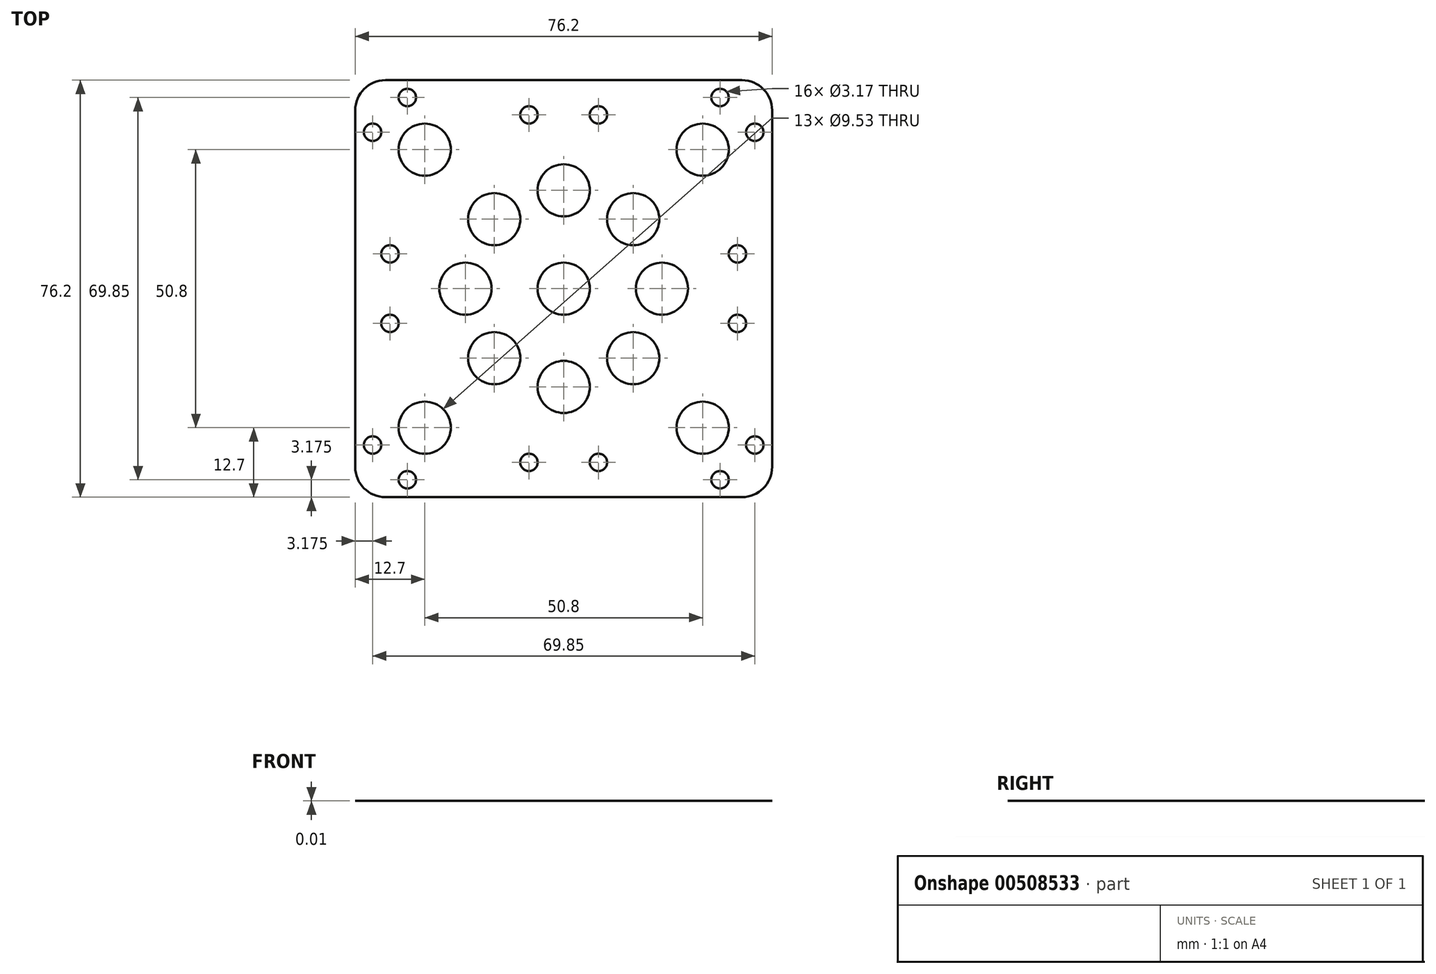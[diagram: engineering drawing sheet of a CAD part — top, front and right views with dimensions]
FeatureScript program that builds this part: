
annotation { "Feature Type Name" : "Feature", "Feature Type Description" : "" }
export const myFeature = defineFeature(function(context is Context, id is Id, definition is map)
    precondition{}
    {
        {
            var Q0;
            Q0=qCreatedBy(makeId("Top.planeOp"),FACE);
            var sketch = newSketch(context, id + "F0", { "sketchPlane" : qUnion([Q0])});
            skLineSegment(sketch, "E0.bottom", {"start": v(38.1, 38.1) * mm, "end": v(-38.1, 38.1) * mm});
            skLineSegment(sketch, "E0.top", {"start": v(38.1, -38.1) * mm, "end": v(-38.1, -38.1) * mm});
            skLineSegment(sketch, "E0.left", {"start": v(38.1, 38.1) * mm, "end": v(38.1, -38.1) * mm});
            skLineSegment(sketch, "E0.right", {"start": v(-38.1, 38.1) * mm, "end": v(-38.1, -38.1) * mm});
            skPoint(sketch, "E0.middle", {"position": v(0, 0) * mm});
            skLineSegment(sketch, "E1.bottom", {"start": v(-25.4, 25.4) * mm, "end": v(25.4, 25.4) * mm, "construction": true});
            skLineSegment(sketch, "E1.top", {"start": v(-25.4, -25.4) * mm, "end": v(25.4, -25.4) * mm, "construction": true});
            skLineSegment(sketch, "E1.left", {"start": v(-25.4, 25.4) * mm, "end": v(-25.4, -25.4) * mm, "construction": true});
            skLineSegment(sketch, "E1.right", {"start": v(25.4, 25.4) * mm, "end": v(25.4, -25.4) * mm, "construction": true});
            skCircle(sketch, "E2", {"center": v(-25.4, 25.4) * mm, "radius": 4.76 * mm});
            skCircle(sketch, "E3", {"center": v(25.4, 25.4) * mm, "radius": 4.76 * mm});
            skCircle(sketch, "E4", {"center": v(25.4, -25.4) * mm, "radius": 4.76 * mm});
            skCircle(sketch, "E5", {"center": v(-25.4, -25.4) * mm, "radius": 4.76 * mm});
            skLineSegment(sketch, "E6.bottom", {"start": v(12.7, 12.7) * mm, "end": v(-12.7, 12.7) * mm, "construction": true});
            skLineSegment(sketch, "E6.top", {"start": v(12.7, -12.7) * mm, "end": v(-12.7, -12.7) * mm, "construction": true});
            skLineSegment(sketch, "E6.left", {"start": v(12.7, 12.7) * mm, "end": v(12.7, -12.7) * mm, "construction": true});
            skLineSegment(sketch, "E6.right", {"start": v(-12.7, 12.7) * mm, "end": v(-12.7, -12.7) * mm, "construction": true});
            skCircle(sketch, "E7", {"center": v(-12.7, 12.7) * mm, "radius": 4.76 * mm});
            skCircle(sketch, "E8", {"center": v(12.7, 12.7) * mm, "radius": 4.76 * mm});
            skCircle(sketch, "E9", {"center": v(12.7, -12.7) * mm, "radius": 4.76 * mm});
            skCircle(sketch, "E10", {"center": v(-12.7, -12.7) * mm, "radius": 4.76 * mm});
            skLineSegment(sketch, "E11", {"start": v(-12.7, 12.7) * mm, "end": v(-38.1, 0) * mm, "construction": true});
            skLineSegment(sketch, "E12", {"start": v(-38.1, 0) * mm, "end": v(-12.7, -12.7) * mm, "construction": true});
            skLineSegment(sketch, "E13", {"start": v(-25.4, 6.35) * mm, "end": v(-38.1, 6.35) * mm, "construction": true});
            skLineSegment(sketch, "E14", {"start": v(-25.4, -6.35) * mm, "end": v(-38.1, -6.35) * mm, "construction": true});
            skPoint(sketch, "E15", {"position": v(-31.75, 6.35) * mm});
            skPoint(sketch, "E16", {"position": v(-31.75, -6.35) * mm});
            skCircle(sketch, "E17", {"center": v(-31.75, 6.35) * mm, "radius": 1.59 * mm});
            skCircle(sketch, "E18", {"center": v(-31.75, -6.35) * mm, "radius": 1.59 * mm});
            skCircle(sketch, "E19.MirrorC", {"center": v(31.75, 6.35) * mm, "radius": 1.59 * mm});
            skCircle(sketch, "E20.MirrorC", {"center": v(31.75, -6.35) * mm, "radius": 1.59 * mm});
            skLineSegment(sketch, "E21", {"start": v(-12.7, 12.7) * mm, "end": v(0, 38.1) * mm, "construction": true});
            skLineSegment(sketch, "E22", {"start": v(-6.35, 25.4) * mm, "end": v(-6.35, 38.1) * mm, "construction": true});
            skCircle(sketch, "E23", {"center": v(-6.35, 31.75) * mm, "radius": 1.59 * mm});
            skCircle(sketch, "E24.MirrorC", {"center": v(6.35, 31.75) * mm, "radius": 1.59 * mm});
            skCircle(sketch, "E25.MirrorC", {"center": v(-6.35, -31.75) * mm, "radius": 1.59 * mm});
            skCircle(sketch, "E26.MirrorC", {"center": v(6.35, -31.75) * mm, "radius": 1.59 * mm});
            skCircle(sketch, "E27", {"center": v(0, 0) * mm, "radius": 4.76 * mm});
            skLineSegment(sketch, "E28", {"start": v(-25.4, 25.4) * mm, "end": v(-38.1, 38.1) * mm, "construction": true});
            skCircle(sketch, "E29.cCircle", {"center": v(0, 0) * mm, "radius": 17.96 * mm, "construction": true});
            skLineSegment(sketch, "E29.0", {"start": v(-17.96, 0) * mm, "end": v(0, 17.96) * mm, "construction": true});
            skLineSegment(sketch, "E29.1", {"start": v(0, 17.96) * mm, "end": v(17.96, 0) * mm, "construction": true});
            skLineSegment(sketch, "E29.2", {"start": v(17.96, 0) * mm, "end": v(0, -17.96) * mm, "construction": true});
            skLineSegment(sketch, "E29.3", {"start": v(0, -17.96) * mm, "end": v(-17.96, 0) * mm, "construction": true});
            skCircle(sketch, "E30", {"center": v(0, 17.96) * mm, "radius": 4.76 * mm});
            skCircle(sketch, "E31", {"center": v(17.96, 0) * mm, "radius": 4.76 * mm});
            skCircle(sketch, "E32", {"center": v(0, -17.96) * mm, "radius": 4.76 * mm});
            skCircle(sketch, "E33", {"center": v(-17.96, 0) * mm, "radius": 4.76 * mm});
            skLineSegment(sketch, "E34", {"start": v(-31.75, 31.75) * mm, "end": v(-38.1, 25.4) * mm, "construction": true});
            skLineSegment(sketch, "E35", {"start": v(-31.75, 31.75) * mm, "end": v(-25.4, 38.1) * mm, "construction": true});
            skPoint(sketch, "E36", {"position": v(-34.92, 28.58) * mm});
            skPoint(sketch, "E37", {"position": v(-28.58, 34.92) * mm});
            skCircle(sketch, "E38", {"center": v(-34.92, 28.58) * mm, "radius": 1.59 * mm});
            skCircle(sketch, "E39", {"center": v(-28.58, 34.92) * mm, "radius": 1.59 * mm});
            skCircle(sketch, "E40.MirrorC", {"center": v(28.58, 34.92) * mm, "radius": 1.59 * mm});
            skCircle(sketch, "E41.MirrorC", {"center": v(34.92, 28.58) * mm, "radius": 1.59 * mm});
            skCircle(sketch, "E42.MirrorC", {"center": v(34.92, -28.58) * mm, "radius": 1.59 * mm});
            skCircle(sketch, "E43.MirrorC", {"center": v(28.58, -34.92) * mm, "radius": 1.59 * mm});
            skCircle(sketch, "E44.MirrorC", {"center": v(-28.58, -34.92) * mm, "radius": 1.59 * mm});
            skCircle(sketch, "E45.MirrorC", {"center": v(-34.92, -28.58) * mm, "radius": 1.59 * mm});
            skSolve(sketch);
        }
        {
            var Q0;
            Q0 = qSketchRegion(id + "F0", true);
            var Q1;
            Q1=makeQuery(id+"F0.imprint","IMPRINT",FACE,{"disambiguationData":[TD([[makeQuery(id+"F0.imprint","IMPRINT",EDGE,{"derivedFrom":sQuery(id+"F0.wireOp",EDGE,"E0.bottom")}),1.0]])]});
            extrude(context, id + "F1", {"entities" : qUnion([Q0, Q1]), "depth" : 1 / 101.6 * mm});
        }
        {
            var Q0;
            Q0=makeQuery(id+"F1.opExtrude","SWEPT_EDGE",EDGE,{"disambiguationData":[OSD([sQuery(id+"F0.wireOp",EDGE,"E0.bottom"),sQuery(id+"F0.wireOp",EDGE,"E0.right")])]});
            var Q1;
            Q1=makeQuery(id+"F1.opExtrude","SWEPT_EDGE",EDGE,{"disambiguationData":[OSD([sQuery(id+"F0.wireOp",EDGE,"E0.top"),sQuery(id+"F0.wireOp",EDGE,"E0.right")])]});
            var Q2;
            Q2=makeQuery(id+"F1.opExtrude","SWEPT_EDGE",EDGE,{"disambiguationData":[OSD([sQuery(id+"F0.wireOp",EDGE,"E0.top"),sQuery(id+"F0.wireOp",EDGE,"E0.left")])]});
            var Q3;
            Q3=makeQuery(id+"F1.opExtrude","SWEPT_EDGE",EDGE,{"disambiguationData":[OSD([sQuery(id+"F0.wireOp",EDGE,"E0.bottom"),sQuery(id+"F0.wireOp",EDGE,"E0.left")])]});
            fillet(context, id + "F2", {"entities" : qUnion([Q0, Q1, Q2, Q3]), "radius" : 5.52 * mm, "tangentPropagation" : true, "allowEdgeOverflow" : false});
        }
    });
